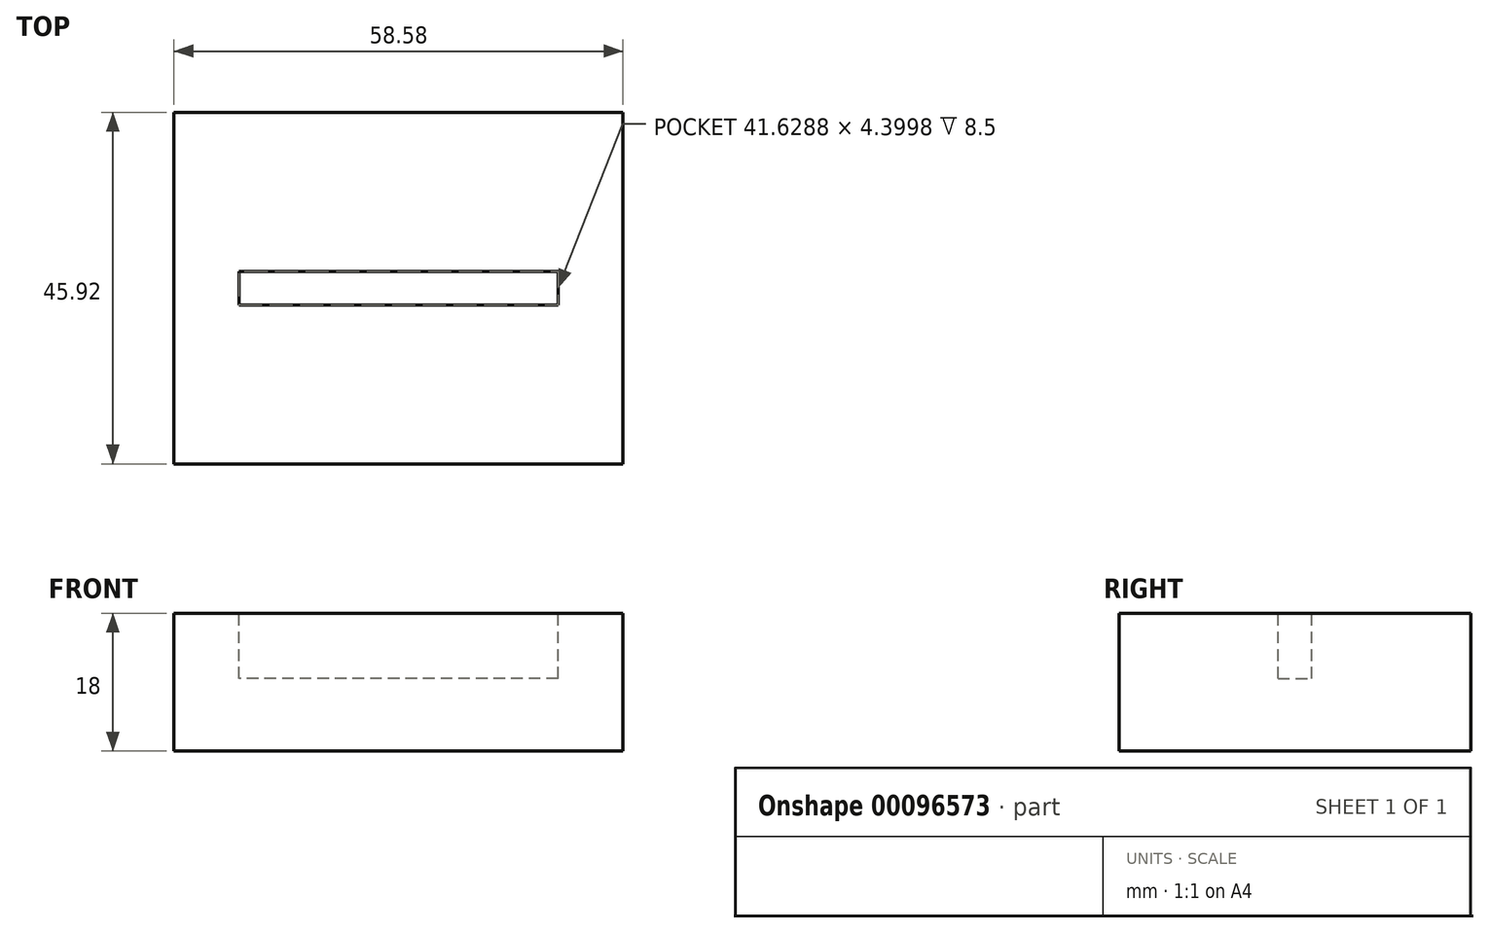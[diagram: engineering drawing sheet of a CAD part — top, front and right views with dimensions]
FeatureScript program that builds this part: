
annotation { "Feature Type Name" : "Feature", "Feature Type Description" : "" }
export const myFeature = defineFeature(function(context is Context, id is Id, definition is map)
    precondition{}
    {
        {
            var Q0;
            Q0=qCreatedBy(makeId("Top.planeOp"),FACE);
            var sketch = newSketch(context, id + "F0", { "sketchPlane" : qUnion([Q0])});
            skLineSegment(sketch, "E0.bottom", {"start": v(-29.29, 22.96) * mm, "end": v(29.29, 22.96) * mm});
            skLineSegment(sketch, "E0.top", {"start": v(-29.29, -22.96) * mm, "end": v(29.29, -22.96) * mm});
            skLineSegment(sketch, "E0.left", {"start": v(-29.29, 22.96) * mm, "end": v(-29.29, -22.96) * mm});
            skLineSegment(sketch, "E0.right", {"start": v(29.29, 22.96) * mm, "end": v(29.29, -22.96) * mm});
            skPoint(sketch, "E0.middle", {"position": v(0, 0) * mm});
            skSolve(sketch);
        }
        {
            var Q0;
            Q0=makeQuery(id+"F0.imprint","IMPRINT",FACE,{"disambiguationData":[TD([[makeQuery(id+"F0.imprint","IMPRINT",EDGE,{"derivedFrom":sQuery(id+"F0.wireOp",EDGE,"E0.bottom")}),-1.0]])]});
            extrude(context, id + "F1", {"entities" : qUnion([Q0]), "depth" : 18 * mm, "symmetric" : true});
        }
        {
            var Q0;
            Q0=makeQuery(id+"F1.opExtrude","CAP_FACE",FACE,{"disambiguationData":[OSD([sQuery(id+"F0.wireOp",EDGE,"E0.bottom"),sQuery(id+"F0.wireOp",EDGE,"E0.top"),sQuery(id+"F0.wireOp",EDGE,"E0.left"),sQuery(id+"F0.wireOp",EDGE,"E0.right")])],"isStart":false});
            var sketch = newSketch(context, id + "F2", { "sketchPlane" : qUnion([Q0])});
            skLineSegment(sketch, "E1.bottom", {"start": v(20.81, -2.2) * mm, "end": v(-20.81, -2.2) * mm});
            skLineSegment(sketch, "E1.top", {"start": v(20.81, 2.2) * mm, "end": v(-20.81, 2.2) * mm});
            skLineSegment(sketch, "E1.left", {"start": v(20.81, -2.2) * mm, "end": v(20.81, 2.2) * mm});
            skLineSegment(sketch, "E1.right", {"start": v(-20.81, -2.2) * mm, "end": v(-20.81, 2.2) * mm});
            skPoint(sketch, "E1.middle", {"position": v(0, 0) * mm});
            skSolve(sketch);
        }
        {
            var Q0;
            Q0=makeQuery(id+"F2.imprint","IMPRINT",FACE,{"disambiguationData":[TD([[makeQuery(id+"F2.imprint","IMPRINT",EDGE,{"derivedFrom":sQuery(id+"F2.wireOp",EDGE,"E1.bottom")}),-1.0]])]});
            extrude(context, id + "F3", {"entities" : qUnion([Q0]), "operationType" : NewBodyOperationType.REMOVE, "oppositeDirection" : true, "depth" : 8.5 * mm});
        }
    });
